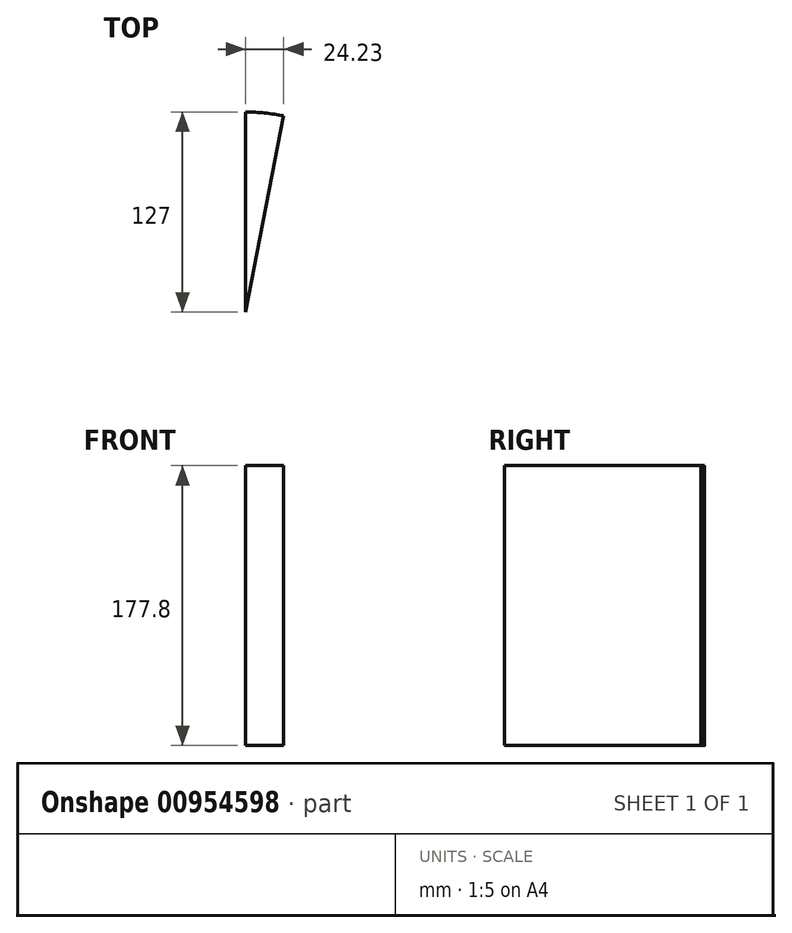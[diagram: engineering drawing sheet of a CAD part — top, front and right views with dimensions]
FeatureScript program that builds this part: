
annotation { "Feature Type Name" : "Feature", "Feature Type Description" : "" }
export const myFeature = defineFeature(function(context is Context, id is Id, definition is map)
    precondition{}
    {
        {
            var Q0;
            Q0=qCreatedBy(makeId("Top.planeOp"),FACE);
            var sketch = newSketch(context, id + "F0", { "sketchPlane" : qUnion([Q0])});
            skCircle(sketch, "E0", {"center": v(0, 0) * mm, "radius": 127 * mm});
            skSolve(sketch);
        }
        {
            var Q0;
            Q0=qCreatedBy(makeId("Top.planeOp"),FACE);
            var sketch = newSketch(context, id + "F1", { "sketchPlane" : qUnion([Q0])});
            skLineSegment(sketch, "E1", {"start": v(0, 0) * mm, "end": v(0, 127) * mm});
            skLineSegment(sketch, "E2", {"start": v(24.23, 124.67) * mm, "end": v(0, 0) * mm});
            skArc(sketch, "E3.0", {"start": v(24.23, 124.67) * mm, "mid": v(12.17, 126.42) * mm, "end": v(0, 127) * mm});
            skSolve(sketch);
        }
        {
            var Q0;
            Q0=makeQuery(id+"F1.imprint","IMPRINT",FACE,{"disambiguationData":[TD([[makeQuery(id+"F1.imprint","IMPRINT",EDGE,{"derivedFrom":sQuery(id+"F1.wireOp",EDGE,"E1")}),-1.0]])]});
            extrude(context, id + "F2", {"entities" : qUnion([Q0]), "depth" : 177.8 * mm, "offsetDistance" : 25.4 * mm});
        }
    });
